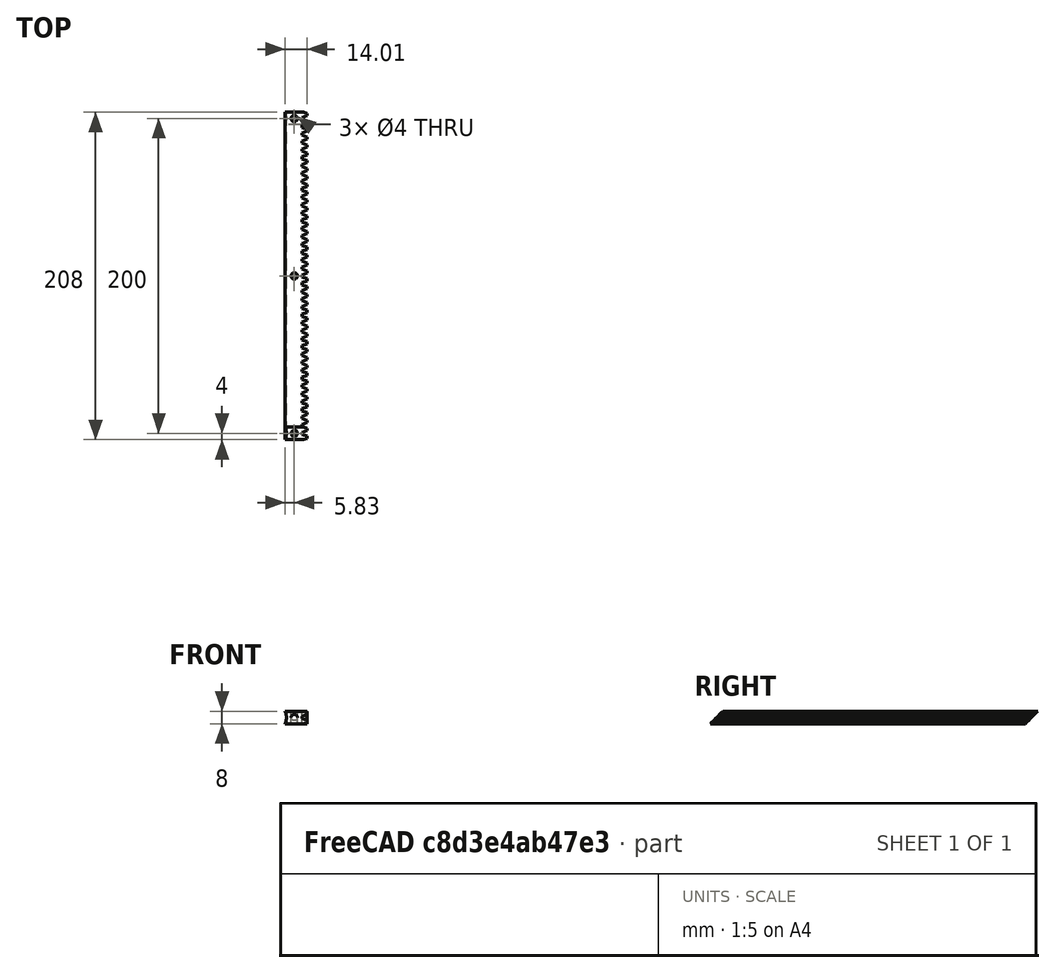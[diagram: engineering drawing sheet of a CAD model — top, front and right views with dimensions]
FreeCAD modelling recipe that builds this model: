
FCSTD DOCUMENT  (FreeCAD 0.18R16110 (Git))
Label: Rack
License: All rights reserved
LicenseURL: http://en.wikipedia.org/wiki/All_rights_reserved
objects: Part::Cylinder×4, Part::Box×3, Part::MultiFuse×2, Part::FeaturePython×1, Part::Cut×1
note: 11 computed .brp shape members not serialized (recipe doc carries the construction recipe); baked Part::Feature solids carry a one-line shape summary decoded from their .brp

FEATURE [Part::Box] Box  label="Cube"
  AttacherType = Attacher::AttachEngine3D
  Height = 8
  Length = 12
  Placement = pos=(-2,0,-4) rot=(0,0,1;0rad)
  Width = 210
FEATURE [Part::Cylinder] Cylinder
  Angle = 360
  AttacherType = Attacher::AttachEngine3D
  Height = 10
  Placement = pos=(5,5,-5) rot=(0,0,1;0rad)
  Radius = 2
FEATURE [Part::Cylinder] Cylinder001
  Angle = 360
  AttacherType = Attacher::AttachEngine3D
  Height = 10
  Placement = pos=(5,105,-5) rot=(0,0,1;0rad)
  Radius = 2
FEATURE [Part::Cylinder] Cylinder002
  Angle = 360
  AttacherType = Attacher::AttachEngine3D
  Height = 10
  Placement = pos=(5,205,-5) rot=(0,0,1;0rad)
  Radius = 2
FEATURE [Part::Cylinder] Cylinder003  label="Rail"
  Angle = 360
  AttacherType = Attacher::AttachEngine3D
  Height = 210
  Placement = pos=(-10,0,0) rot=(-1,0,0;1.5708rad)
  Radius = 10
FEATURE [Part::Box] Box001  label="Cube001"
  AttacherType = Attacher::AttachEngine3D
  Height = 20
  Length = 20
  Placement = pos=(-5,10,5) rot=(1,0,0;2.35619rad)
  Width = 10
FEATURE [Part::Box] Box002  label="Cube002"
  AttacherType = Attacher::AttachEngine3D
  Height = 20
  Length = 20
  Placement = pos=(-5,200,-5) rot=(-1,0,0;0.785398rad)
  Width = 10
FEATURE [Part::MultiFuse] Fusion001  label="Negative Fusion"
  Shapes = -> [Cylinder,Cylinder001,Cylinder002,Cylinder003,Box001,Box002]
FEATURE [Part::FeaturePython] InvoluteRack001  # WARN: FeaturePython — macro-defined, semantics opaque (R4)
  Placement = pos=(11.5915,2.5,-4) rot=(0,0,1;0rad)
  beta = 0
  double_helix = false
  head = 0
  height = 8
  module = 1.59155
  pressure_angle = 20
  teeth = 42
  thickness = 1
  expr: module = 5 / pi
  expr: Placement.Base.x = 10 + 5 / pi
FEATURE [Part::MultiFuse] Fusion  label="Positive Fusion"
  Shapes = -> [Box,InvoluteRack001]
FEATURE [Part::Cut] Cut
  Base = -> Fusion
  Tool = -> Fusion001
